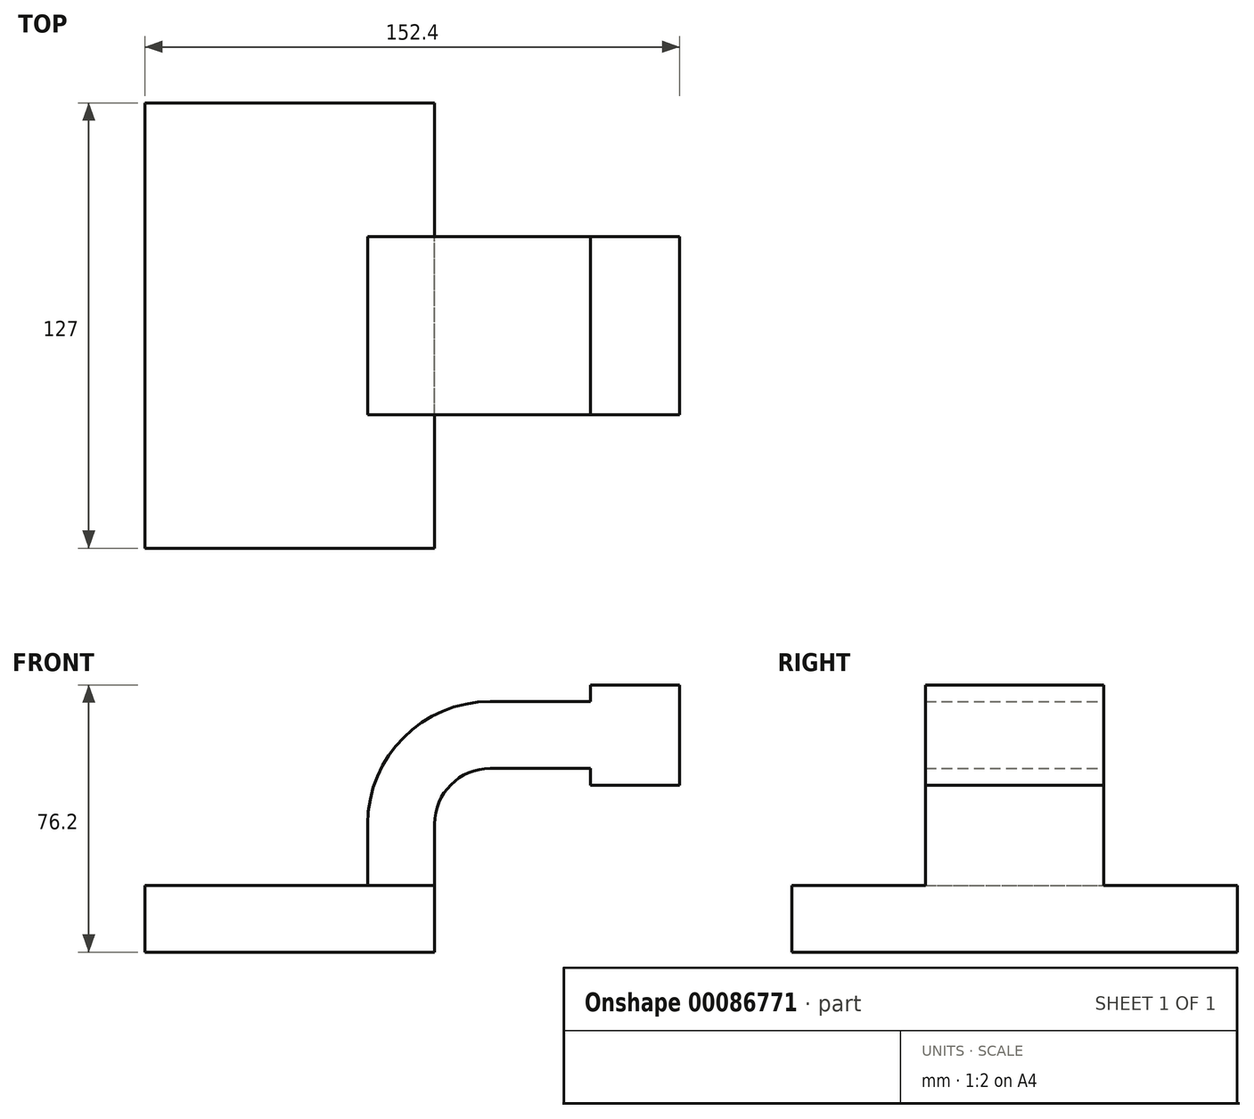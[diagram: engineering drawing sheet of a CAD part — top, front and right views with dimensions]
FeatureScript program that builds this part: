
annotation { "Feature Type Name" : "Feature", "Feature Type Description" : "" }
export const myFeature = defineFeature(function(context is Context, id is Id, definition is map)
    precondition{}
    {
        {
            var Q0;
            Q0=qCreatedBy(makeId("Front.planeOp"),FACE);
            var sketch = newSketch(context, id + "F0", { "sketchPlane" : qUnion([Q0])});
            skLineSegment(sketch, "E0.bottom", {"start": v(41.28, -9.53) * mm, "end": v(-41.28, -9.53) * mm});
            skLineSegment(sketch, "E0.top", {"start": v(41.28, 9.53) * mm, "end": v(-41.28, 9.53) * mm});
            skLineSegment(sketch, "E0.left", {"start": v(41.28, -9.52) * mm, "end": v(41.28, 9.53) * mm});
            skLineSegment(sketch, "E0.right", {"start": v(-41.27, -9.52) * mm, "end": v(-41.27, 9.53) * mm});
            skPoint(sketch, "E0.middle", {"position": v(0, 0) * mm});
            skLineSegment(sketch, "E1.bottom", {"start": v(111.12, 38.1) * mm, "end": v(60.32, 38.1) * mm});
            skLineSegment(sketch, "E1.top", {"start": v(111.12, 66.68) * mm, "end": v(60.32, 66.68) * mm});
            skLineSegment(sketch, "E1.left", {"start": v(111.12, 38.1) * mm, "end": v(111.12, 66.68) * mm});
            skLineSegment(sketch, "E1.right", {"start": v(60.32, 38.1) * mm, "end": v(60.32, 66.68) * mm});
            skPoint(sketch, "E1.middle", {"position": v(85.72, 52.39) * mm});
            skLineSegment(sketch, "E2", {"start": v(41.28, 9.53) * mm, "end": v(41.28, 26.99) * mm});
            skArc(sketch, "E3", {"start": v(41.27, 26.99) * mm, "mid": v(45.92, 38.21) * mm, "end": v(57.15, 42.86) * mm});
            skLineSegment(sketch, "E4", {"start": v(57.15, 42.86) * mm, "end": v(85.72, 42.86) * mm});
            skLineSegment(sketch, "E5.0", {"start": v(57.15, 61.91) * mm, "end": v(85.72, 61.91) * mm});
            skArc(sketch, "E5.1", {"start": v(22.23, 26.99) * mm, "mid": v(32.45, 51.68) * mm, "end": v(57.15, 61.91) * mm});
            skLineSegment(sketch, "E5.2", {"start": v(22.22, 9.53) * mm, "end": v(22.22, 26.99) * mm});
            skLineSegment(sketch, "E6", {"start": v(85.72, 38.1) * mm, "end": v(85.72, 66.68) * mm});
            skFitSpline(sketch, "E7", {"points": [v(-41.27, 9.53) * mm, v(57.15, 61.91) * mm], "startDerivative": vector(0, 86.07) * mm, "endDerivative": vector(139.56, 0) * mm});
            skSolve(sketch);
        }
        {
            var Q0;
            Q0=makeQuery(id+"F0.imprint","IMPRINT",FACE,{"disambiguationData":[TD([[makeQuery(id+"F0.imprint","IMPRINT",EDGE,{"derivedFrom":sQuery(id+"F0.wireOp",EDGE,"E0.bottom")}),-1.0]])]});
            extrude(context, id + "F1", {"entities" : qUnion([Q0]), "endBound" : BoundingType.SYMMETRIC, "depth" : 127 * mm});
        }
        {
            var Q0;
            {var subQ1=sQuery(id+"F0.wireOp",EDGE,"E2");Q0=makeQuery(id+"F0.imprint","IMPRINT",FACE,{"disambiguationData":[TD([[makeQuery(id+"F0.imprint","IMPRINT",EDGE,{"derivedFrom":subQ1}),1.0]])]});}
            var Q1;
            {var subQ0=sQuery(id+"F0.wireOp",EDGE,"E4");var subQ1=sQuery(id+"F0.wireOp",EDGE,"E1.right");var subQ2=makeQuery(id+"F0.imprint","INTERSECT",VERTEX,{"derivedFrom":[subQ1,subQ0]});Q1=makeQuery(id+"F0.imprint","IMPRINT",FACE,{"disambiguationData":[TD([[makeQuery(id+"F0.imprint","IMPRINT",EDGE,{"disambiguationData":[TD([[subQ2,-1.0]])],"derivedFrom":subQ1}),-1.0]])]});}
            var Q2;
            {var subQ0=sQuery(id+"F0.wireOp",EDGE,"E1.left");Q2=makeQuery(id+"F0.imprint","IMPRINT",FACE,{"disambiguationData":[TD([[makeQuery(id+"F0.imprint","IMPRINT",EDGE,{"derivedFrom":subQ0}),1.0]])]});}
            extrude(context, id + "F2", {"entities" : qUnion([Q0, Q1, Q2]), "operationType" : NewBodyOperationType.ADD, "endBound" : BoundingType.SYMMETRIC, "depth" : 50.8 * mm});
        }
        {
            var Q0;
            Q0=makeQuery(id+"F0.imprint","IMPRINT",FACE,{"disambiguationData":[TD([[makeQuery(id+"F0.imprint","IMPRINT",EDGE,{"derivedFrom":sQuery(id+"F0.wireOp",EDGE,"E5.1")}),1.0]])]});
            extrude(context, id + "F3", {"entities" : qUnion([Q0]), "operationType" : NewBodyOperationType.ADD, "endBound" : BoundingType.SYMMETRIC, "depth" : 15.88 * mm});
        }
    });
